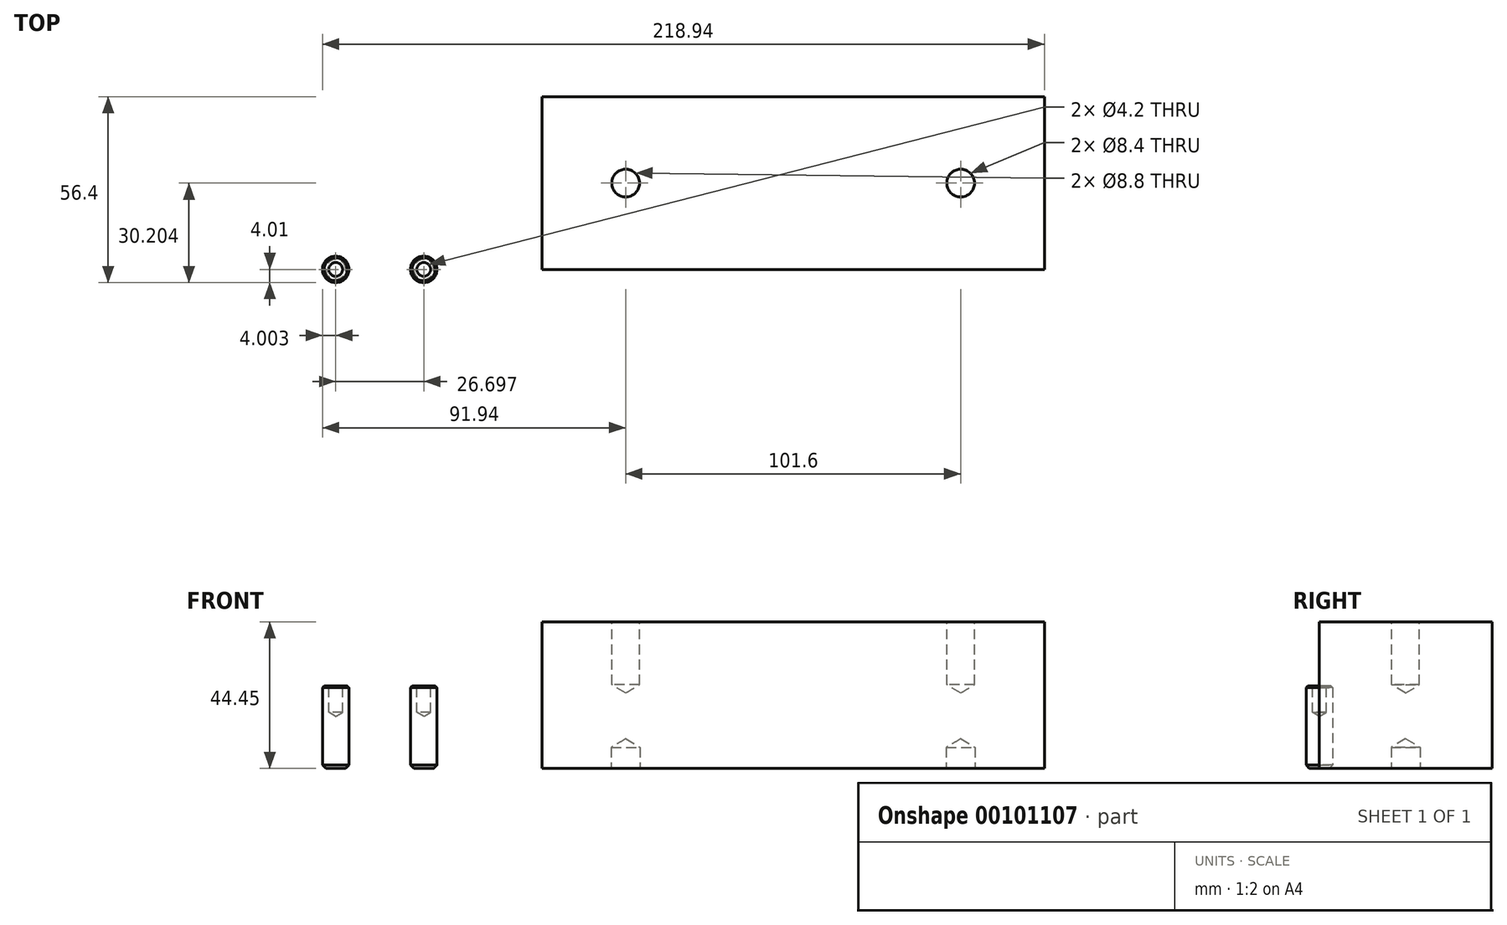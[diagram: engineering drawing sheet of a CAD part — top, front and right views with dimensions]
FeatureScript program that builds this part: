
annotation { "Feature Type Name" : "Feature", "Feature Type Description" : "" }
export const myFeature = defineFeature(function(context is Context, id is Id, definition is map)
    precondition{}
    {
        {
            var Q0;
            Q0=qCreatedBy(makeId("Top.planeOp"),FACE);
            var sketch = newSketch(context, id + "F0", { "sketchPlane" : qUnion([Q0])});
            skLineSegment(sketch, "E0.bottom", {"start": v(0, 0) * mm, "end": v(152.4, 0) * mm});
            skLineSegment(sketch, "E0.top", {"start": v(0, 52.39) * mm, "end": v(152.4, 52.39) * mm});
            skLineSegment(sketch, "E0.left", {"start": v(0, 0) * mm, "end": v(0, 52.39) * mm});
            skLineSegment(sketch, "E0.right", {"start": v(152.4, 0) * mm, "end": v(152.4, 52.39) * mm});
            skSolve(sketch);
        }
        {
            var Q0;
            Q0=makeQuery(id+"F0.imprint","IMPRINT",FACE,{"disambiguationData":[TD([[makeQuery(id+"F0.imprint","IMPRINT",EDGE,{"derivedFrom":sQuery(id+"F0.wireOp",EDGE,"E0.bottom")}),1.0]])]});
            extrude(context, id + "F1", {"entities" : qUnion([Q0]), "depth" : 44.45 * mm});
        }
        {
            var Q0;
            Q0=makeQuery(id+"F1.opExtrude","CAP_FACE",FACE,{"disambiguationData":[OSD([sQuery(id+"F0.wireOp",EDGE,"E0.bottom"),sQuery(id+"F0.wireOp",EDGE,"E0.top"),sQuery(id+"F0.wireOp",EDGE,"E0.left"),sQuery(id+"F0.wireOp",EDGE,"E0.right")])],"isStart":false});
            var sketch = newSketch(context, id + "F2", { "sketchPlane" : qUnion([Q0])});
            skLineSegment(sketch, "E1", {"start": v(76.2, 26.2) * mm, "end": v(25.4, 26.2) * mm});
            skPoint(sketch, "E1.startSnap0", {"position": v(0, 26.2) * mm});
            skPoint(sketch, "E1.startSnap1", {"position": v(76.2, 0) * mm});
            skLineSegment(sketch, "E2", {"start": v(25.4, 26.2) * mm, "end": v(127, 26.2) * mm});
            skSolve(sketch);
        }
        {
            var Q0;
            Q0=sQuery(id+"F2.wireOp",VERTEX,"E2.start");
            var Q1;
            Q1=sQuery(id+"F2.wireOp",VERTEX,"E2.end");
            var Q2;
            Q2=makeQuery(id+"F1.opExtrude","SWEPT_BODY",BODY,{"disambiguationData":[OSD([sQuery(id+"F0.wireOp",EDGE,"E0.bottom"),sQuery(id+"F0.wireOp",EDGE,"E0.top"),sQuery(id+"F0.wireOp",EDGE,"E0.left"),sQuery(id+"F0.wireOp",EDGE,"E0.right")])]});
            hole(context, id + "F3", {"style" : HoleStyle.SIMPLE, "endStyle" : HoleEndStyle.BLIND, "standardTappedOrClearance" : lookupTablePath({ "standard" : "ISO", "fit" : "Close", "size" : "M8", "type" : "Clearance" }), "standardBlindInLast" : lookupTablePath({ "fit" : "Close", "standard" : "ISO", "size" : "M8", "type" : "Clearance" }), "holeDiameter" : 8.4 * mm, "holeDepth" : 19.05 * mm, "locations" : qUnion([Q0, Q1]), "scope" : qUnion([Q2])});
        }
        {
            var Q0;
            Q0=qCreatedBy(makeId("Front.planeOp"),FACE);
            var sketch = newSketch(context, id + "F4", { "sketchPlane" : qUnion([Q0])});
            skLineSegment(sketch, "E3.bottom", {"start": v(-66.54, 0) * mm, "end": v(-62.54, 0) * mm});
            skLineSegment(sketch, "E3.top", {"start": v(-66.54, 25) * mm, "end": v(-62.54, 25) * mm});
            skLineSegment(sketch, "E3.left", {"start": v(-66.54, 0) * mm, "end": v(-66.54, 25) * mm});
            skLineSegment(sketch, "E3.right", {"start": v(-62.54, 0) * mm, "end": v(-62.54, 25) * mm});
            skSolve(sketch);
        }
        {
            var Q0;
            Q0=makeQuery(id+"F4.imprint","IMPRINT",FACE,{"disambiguationData":[TD([[makeQuery(id+"F4.imprint","IMPRINT",EDGE,{"derivedFrom":sQuery(id+"F4.wireOp",EDGE,"E3.bottom")}),1.0]])]});
            var Q1;
            Q1=sQuery(id+"F4.wireOp",EDGE,"E3.right");
            revolve(context, id + "F5", {"entities" : qUnion([Q0]), "axis" : qUnion([Q1]), "revolveType" : RevolveType.FULL});
        }
        {
            var Q0;
            Q0=makeQuery(id+"F5.opRevolve","SWEPT_EDGE",EDGE,{"disambiguationData":[OSD([sQuery(id+"F4.wireOp",EDGE,"E3.top"),sQuery(id+"F4.wireOp",EDGE,"E3.left")])]});
            chamfer(context, id + "F6", {"entities" : qUnion([Q0]), "width" : .5 * mm, "tangentPropagation" : true});
        }
        {
            var Q0;
            Q0=makeQuery(id+"F5.opRevolve","SWEPT_EDGE",EDGE,{"disambiguationData":[OSD([sQuery(id+"F4.wireOp",EDGE,"E3.bottom"),sQuery(id+"F4.wireOp",EDGE,"E3.left")])]});
            chamfer(context, id + "F7", {"entities" : qUnion([Q0]), "width" : 1 * mm, "tangentPropagation" : true});
        }
        {
            var Q0;
            Q0=makeQuery(id+"F5.opRevolve","SWEPT_FACE",FACE,{"disambiguationData":[OSD([sQuery(id+"F4.wireOp",EDGE,"E3.top")])]});
            var sketch = newSketch(context, id + "F8", { "sketchPlane" : qUnion([Q0])});
            skPoint(sketch, "E4", {"position": v(-62.54, 0) * mm});
            skSolve(sketch);
        }
        {
            var Q0;
            Q0=sQuery(id+"F8.wireOp",VERTEX,"E4");
            var Q1;
            Q1=makeQuery(id+"F5.opRevolve","SWEPT_BODY",BODY,{"disambiguationData":[OSD([sQuery(id+"F4.wireOp",EDGE,"E3.bottom"),sQuery(id+"F4.wireOp",EDGE,"E3.top"),sQuery(id+"F4.wireOp",EDGE,"E3.left"),sQuery(id+"F4.wireOp",EDGE,"E3.right")])]});
            hole(context, id + "F9", {"style" : HoleStyle.SIMPLE, "endStyle" : HoleEndStyle.BLIND, "standardTappedOrClearance" : lookupTablePath({ "standard" : "ISO", "engagement" : "75%", "pitch" : "0.8 mm", "size" : "M5", "type" : "Tapped" }), "standardBlindInLast" : lookupTablePath({ "standard" : "ISO", "engagement" : "75%", "pitch" : "0.8 mm", "size" : "M5", "type" : "Tapped" }), "holeDiameter" : 4.2 * mm, "holeDepth" : 8 * mm, "locations" : qUnion([Q0]), "scope" : qUnion([Q1]), "majorDiameter" : 5 * mm});
        }
        {
            var Q0;
            Q0=makeQuery(id+"F5.opRevolve","SWEPT_BODY",BODY,{"disambiguationData":[OSD([sQuery(id+"F4.wireOp",EDGE,"E3.bottom"),sQuery(id+"F4.wireOp",EDGE,"E3.top"),sQuery(id+"F4.wireOp",EDGE,"E3.left"),sQuery(id+"F4.wireOp",EDGE,"E3.right")])]});
            transform(context, id + "F10", {"entities" : qUnion([Q0]), "transformType" : TransformType.TRANSLATION_3D, "dx" : 26.7 * mm, "dy" : 0 * mm, "dz" : 0 * mm, "makeCopy" : true});
        }
        {
            var Q0;
            Q0=makeQuery(id+"F1.opExtrude","CAP_FACE",FACE,{"disambiguationData":[OSD([sQuery(id+"F0.wireOp",EDGE,"E0.bottom"),sQuery(id+"F0.wireOp",EDGE,"E0.top"),sQuery(id+"F0.wireOp",EDGE,"E0.left"),sQuery(id+"F0.wireOp",EDGE,"E0.right")])],"isStart":true});
            var sketch = newSketch(context, id + "F11", { "sketchPlane" : qUnion([Q0])});
            skLineSegment(sketch, "E5", {"start": v(76.2, -26.2) * mm, "end": v(25.4, -26.2) * mm});
            skPoint(sketch, "E5.startSnap0", {"position": v(76.2, 0) * mm});
            skPoint(sketch, "E5.startSnap1", {"position": v(0, -26.2) * mm});
            skLineSegment(sketch, "E6", {"start": v(25.4, -26.2) * mm, "end": v(127, -26.2) * mm});
            skSolve(sketch);
        }
        {
            var Q0;
            Q0=sQuery(id+"F11.wireOp",VERTEX,"E6.start");
            var Q1;
            Q1=sQuery(id+"F11.wireOp",VERTEX,"E6.end");
            var Q2;
            Q2=makeQuery(id+"F1.opExtrude","SWEPT_BODY",BODY,{"disambiguationData":[OSD([sQuery(id+"F0.wireOp",EDGE,"E0.bottom"),sQuery(id+"F0.wireOp",EDGE,"E0.top"),sQuery(id+"F0.wireOp",EDGE,"E0.left"),sQuery(id+"F0.wireOp",EDGE,"E0.right")])]});
            hole(context, id + "F12", {"style" : HoleStyle.SIMPLE, "endStyle" : HoleEndStyle.BLIND, "standardTappedOrClearance" : lookupTablePath({ "standard" : "ISO", "fit" : "Normal", "size" : "M8", "type" : "Clearance" }), "standardBlindInLast" : lookupTablePath({ "fit" : "Standard", "standard" : "ISO", "size" : "M8", "type" : "Clearance" }), "holeDiameter" : 8.8 * mm, "holeDepth" : 6.35 * mm, "locations" : qUnion([Q0, Q1]), "scope" : qUnion([Q2])});
        }
    });
